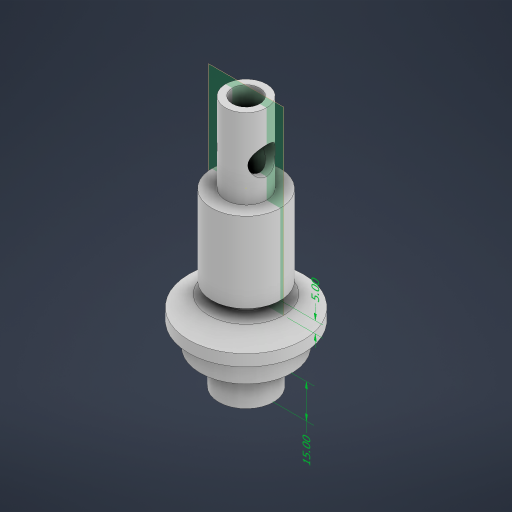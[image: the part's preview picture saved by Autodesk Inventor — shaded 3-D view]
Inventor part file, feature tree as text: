
AUTODESK INVENTOR PART (.ipt)
format: ipt  version: 2024.3 (Build 283343000, 343)  size: 278,528 bytes
history: native  units: mm
features: sketch x10, extrude x8, other x3, plane x1, revolve x1, move_body x1
ambient origin geometry x8: Origin, YZ Plane, XZ Plane, XY Plane, X Axis, Y Axis, Z Axis, Center Point
bodies: Solid1 (feature_tree)
feature tree (24):
  other  "Annotations"
  extrude  "Extrusion1"  Depth=35.0mm TaperAngle=0.0deg
  extrude  "Extrusion2"  Depth=35.0mm TaperAngle=0.0deg
  extrude  "Extrusion3"  Depth=5.0mm
  plane  "Work Plane1"
  sketch  "Sketch7"  dims[d22=25.0mm d23=90.0deg]
  revolve  "Revolution1"  Angle=90.0deg
  extrude  "Extrusion5"  Depth=40.0mm
  extrude  "Extrusion6"  Depth=10.0mm
  extrude  "Extrusion7"  Depth=15.0mm
  extrude  "Extrusion8"  Depth=12.0mm
  extrude  "Extrusion9"  Depth=15.0mm TaperAngle=0.0deg
  move_body  "Move Body2"
  sketch  "Sketch2"  dims[d0=18.0mm d1=35.0mm d2=0.0mm]
  sketch  "Sketch3"  dims[d3=30.0mm d4=35.0mm d5=0.0mm]
  sketch  "Sketch4"  dims[d6=5.0mm d7=0.0mm d21=5.0mm]
  sketch  "Sketch8"  dims[d24=5.0mm d25=0.0mm d26=40.0mm]
  sketch  "Sketch9"  dims[d27=10.0mm d28=0.0mm d29=24.0mm]
  sketch  "Sketch10"  dims[d30=15.0mm d31=0.0mm d32=12.0mm]
  sketch  "Sketch11"  dims[d33=120.0mm d34=0.0mm d45=12.0mm]
  sketch  "Sketch12"  dims[d47=15.0mm d48=18.0mm d49=0.0mm]
  sketch  "Sketch13"  dims[d55=90.0deg d38=5.0mm d41=15.0mm]
  other  "Linear Dimension 4"
  other  "Linear Dimension 7"
